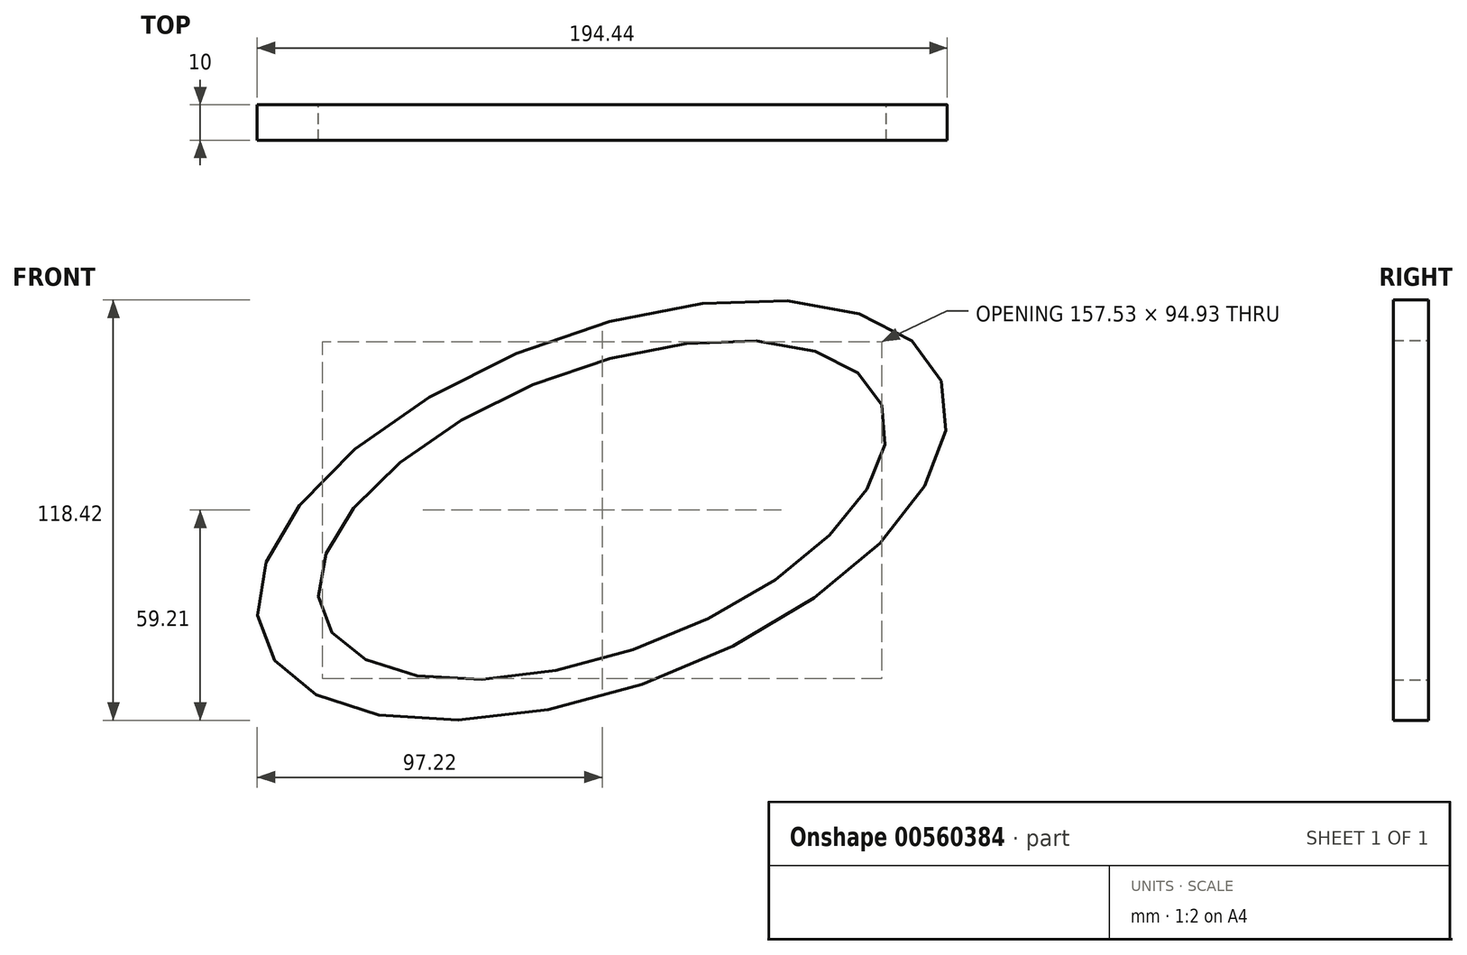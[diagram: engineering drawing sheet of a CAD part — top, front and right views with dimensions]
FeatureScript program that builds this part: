
annotation { "Feature Type Name" : "Feature", "Feature Type Description" : "" }
export const myFeature = defineFeature(function(context is Context, id is Id, definition is map)
    precondition{}
    {
        {
            var Q0;
            Q0=qCreatedBy(makeId("Front.planeOp"),FACE);
            var sketch = newSketch(context, id + "F0", { "sketchPlane" : qUnion([Q0])});
            skEllipse(sketch, "E0", {"center": v(0, 0) * mm, "majorRadius": 102.26 * mm, "minorRadius": 50 * mm, "majorAxis": v(0.93, 0.36)});
            skEllipse(sketch, "E1", {"center": v(0, 0) * mm, "majorRadius": 84.18 * mm, "minorRadius": 40 * mm, "majorAxis": v(0.94, 0.35)});
            skSolve(sketch);
        }
        {
            var Q0;
            Q0=makeQuery(id+"F0.imprint","IMPRINT",FACE,{"disambiguationData":[TD([[makeQuery(id+"F0.imprint","IMPRINT",EDGE,{"derivedFrom":sQuery(id+"F0.wireOp",EDGE,"E0")}),1.0]])]});
            extrude(context, id + "F1", {"entities" : qUnion([Q0]), "depth" : 10 * mm, "offsetDistance" : 25 * mm});
        }
    });
